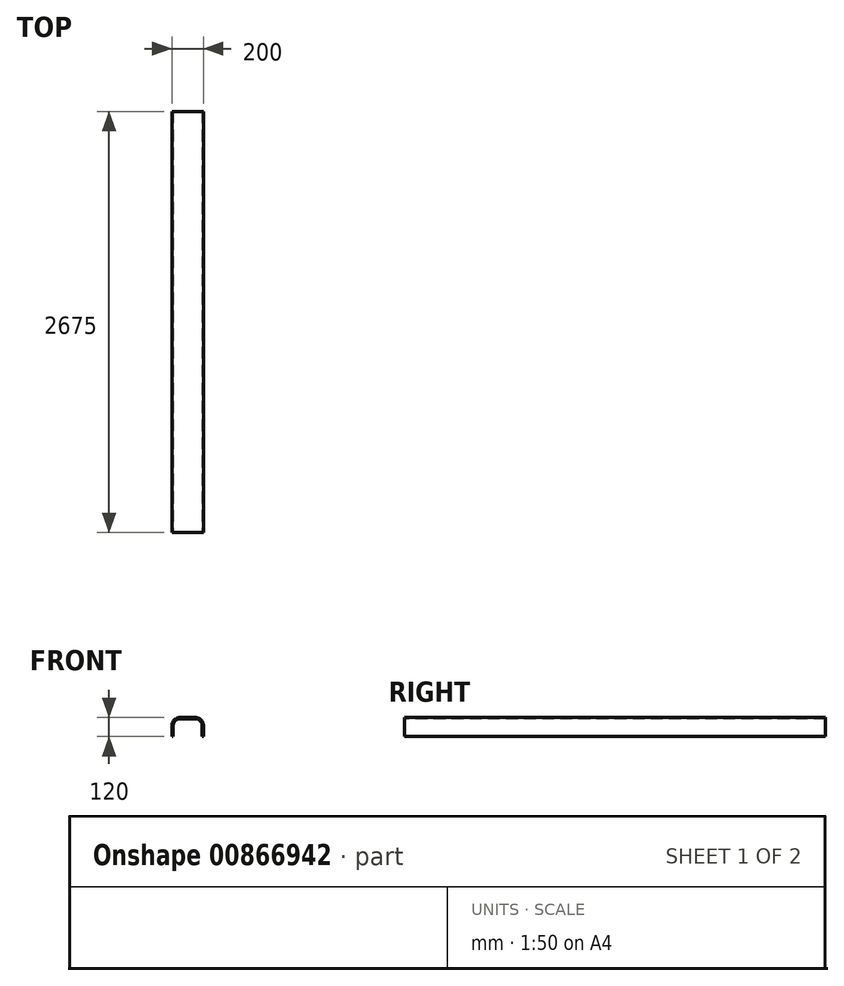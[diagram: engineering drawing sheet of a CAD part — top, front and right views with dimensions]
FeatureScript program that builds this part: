
annotation { "Feature Type Name" : "Feature", "Feature Type Description" : "" }
export const myFeature = defineFeature(function(context is Context, id is Id, definition is map)
    precondition{}
    {
        {
            var Q0;
            Q0=qCreatedBy(makeId("Front.planeOp"),FACE);
            var sketch = newSketch(context, id + "F0", { "sketchPlane" : qUnion([Q0])});
            skLineSegment(sketch, "E0", {"start": v(-100, 0) * mm, "end": v(-100, 70) * mm});
            skLineSegment(sketch, "E1", {"start": v(-50, 120) * mm, "end": v(0, 120) * mm});
            skPoint(sketch, "E2.visualSharp", {"position": v(-100, 120) * mm});
            skArc(sketch, "E2.filletArc", {"start": v(-50, 120) * mm, "mid": v(-85.36, 105.36) * mm, "end": v(-100, 70) * mm});
            skLineSegment(sketch, "E3.0", {"start": v(-50, 112) * mm, "end": v(0, 112) * mm});
            skArc(sketch, "E3.1", {"start": v(-50, 112) * mm, "mid": v(-79.7, 99.7) * mm, "end": v(-92, 70) * mm});
            skLineSegment(sketch, "E3.2", {"start": v(-92, 0) * mm, "end": v(-92, 70) * mm});
            skLineSegment(sketch, "E4", {"start": v(0, 0) * mm, "end": v(0, 220.37) * mm, "construction": true});
            skLineSegment(sketch, "E5", {"start": v(-100, 0) * mm, "end": v(-92, 0) * mm});
            skLineSegment(sketch, "E6.MirrorCS", {"start": v(100, 0) * mm, "end": v(92, 0) * mm});
            skLineSegment(sketch, "E7.MirrorCS", {"start": v(100, 0) * mm, "end": v(100, 70) * mm});
            skLineSegment(sketch, "E8.MirrorCS", {"start": v(92, 0) * mm, "end": v(92, 70) * mm});
            skLineSegment(sketch, "E9.MirrorCS", {"start": v(50, 120) * mm, "end": v(0, 120) * mm});
            skLineSegment(sketch, "E10.MirrorCS", {"start": v(50, 112) * mm, "end": v(0, 112) * mm});
            skArc(sketch, "E11.MirrorCS", {"start": v(50, 112) * mm, "mid": v(79.7, 99.7) * mm, "end": v(92, 70) * mm});
            skArc(sketch, "E12.MirrorCS", {"start": v(50, 120) * mm, "mid": v(85.36, 105.36) * mm, "end": v(100, 70) * mm});
            skSolve(sketch);
        }
        {
            var Q0;
            Q0 = qSketchRegion(id + "F0", true);
            extrude(context, id + "F1", {"entities" : qUnion([Q0]), "oppositeDirection" : true, "depth" : 2675 * mm, "offsetDistance" : 25 * mm});
        }
    });
